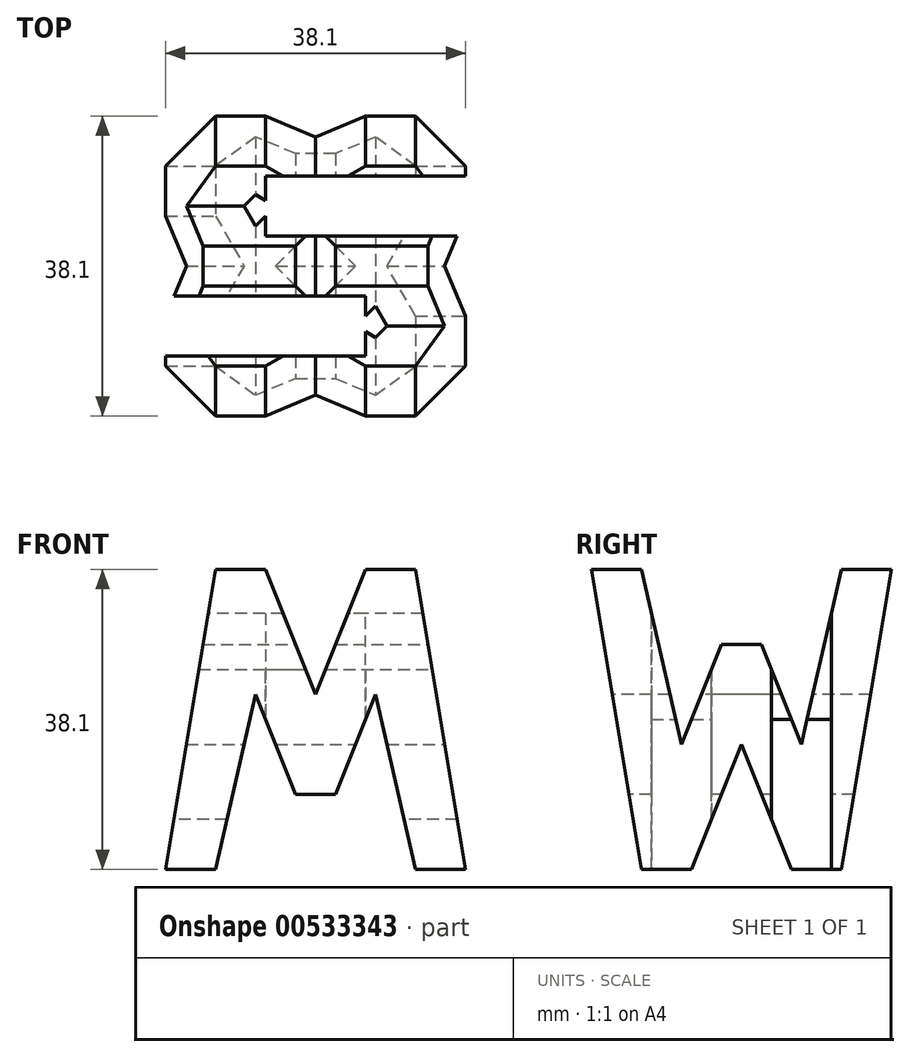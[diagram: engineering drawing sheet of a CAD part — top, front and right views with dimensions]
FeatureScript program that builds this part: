
annotation { "Feature Type Name" : "Feature", "Feature Type Description" : "" }
export const myFeature = defineFeature(function(context is Context, id is Id, definition is map)
    precondition{}
    {
        {
            var Q0;
            Q0=qCreatedBy(makeId("Front.planeOp"),FACE);
            var sketch = newSketch(context, id + "F0", { "sketchPlane" : qUnion([Q0])});
            skLineSegment(sketch, "E0", {"start": v(0, 0) * mm, "end": v(0, 38.1) * mm});
            skLineSegment(sketch, "E1", {"start": v(0, 38.1) * mm, "end": v(38.1, 38.1) * mm});
            skLineSegment(sketch, "E2", {"start": v(38.1, 38.1) * mm, "end": v(38.1, 0) * mm});
            skLineSegment(sketch, "E3", {"start": v(0, 0) * mm, "end": v(38.1, 0) * mm});
            skSolve(sketch);
        }
        {
            var Q0;
            Q0 = qSketchRegion(id + "F0", true);
            extrude(context, id + "F1", {"entities" : qUnion([Q0]), "depth" : 38.1 * mm, "offsetDistance" : 25.4 * mm});
        }
        {
            var Q0;
            Q0=qCreatedBy(makeId("Front.planeOp"),FACE);
            cPlane(context, id + "F2", {"entities" : qUnion([Q0]), "cplaneType" : CPlaneType.OFFSET, "offset" : 38.1 * mm, "width" : 152.4 * mm, "height" : 152.4 * mm});
        }
        {
            var Q0;
            Q0=qCreatedBy(makeId("Right.planeOp"),FACE);
            cPlane(context, id + "F3", {"entities" : qUnion([Q0]), "cplaneType" : CPlaneType.OFFSET, "offset" : 38.1 * mm, "width" : 152.4 * mm, "height" : 152.4 * mm});
        }
        {
            var Q0;
            Q0=qCreatedBy(makeId("Top.planeOp"),FACE);
            cPlane(context, id + "F4", {"entities" : qUnion([Q0]), "cplaneType" : CPlaneType.OFFSET, "offset" : 38.1 * mm, "width" : 152.4 * mm, "height" : 152.4 * mm});
        }
        {
            var Q0;
            Q0=qCreatedBy(id+"F3.planeOp",FACE);
            var sketch = newSketch(context, id + "F5", { "sketchPlane" : qUnion([Q0])});
            skLineSegment(sketch, "E4", {"start": v(-38.1, 38.1) * mm, "end": v(-38.1, 0) * mm});
            skLineSegment(sketch, "E5", {"start": v(-38.1, 0) * mm, "end": v(0, 0) * mm});
            skLineSegment(sketch, "E6", {"start": v(0, 0) * mm, "end": v(0, 38.1) * mm});
            skLineSegment(sketch, "E7", {"start": v(0, 38.1) * mm, "end": v(-38.1, 38.1) * mm});
            skLineSegment(sketch, "E8", {"start": v(-38.1, 38.1) * mm, "end": v(-31.75, 0) * mm});
            skLineSegment(sketch, "E9", {"start": v(-31.75, 0) * mm, "end": v(-25.4, 0) * mm});
            skLineSegment(sketch, "E10", {"start": v(-25.4, 0) * mm, "end": v(-19.05, 15.87) * mm});
            skLineSegment(sketch, "E11", {"start": v(-19.05, 15.87) * mm, "end": v(-12.7, 0) * mm});
            skLineSegment(sketch, "E12", {"start": v(-12.7, 0) * mm, "end": v(-6.35, 0) * mm});
            skLineSegment(sketch, "E13", {"start": v(-6.35, 0) * mm, "end": v(0, 38.1) * mm});
            skLineSegment(sketch, "E14", {"start": v(0, 38.1) * mm, "end": v(-6.35, 38.1) * mm});
            skLineSegment(sketch, "E15", {"start": v(-6.35, 38.1) * mm, "end": v(-11.43, 15.87) * mm});
            skLineSegment(sketch, "E16", {"start": v(-11.43, 15.87) * mm, "end": v(-16.51, 28.57) * mm});
            skLineSegment(sketch, "E17", {"start": v(-16.51, 28.57) * mm, "end": v(-21.6, 28.57) * mm});
            skLineSegment(sketch, "E18", {"start": v(-21.6, 28.57) * mm, "end": v(-26.67, 15.87) * mm});
            skLineSegment(sketch, "E19", {"start": v(-26.67, 15.87) * mm, "end": v(-31.75, 38.1) * mm});
            skSolve(sketch);
        }
        {
            var Q0;
            {var subQ0=sQuery(id+"F5.wireOp",EDGE,"E15");Q0=makeQuery(id+"F5.imprint","IMPRINT",FACE,{"disambiguationData":[TD([[makeQuery(id+"F5.imprint","IMPRINT",EDGE,{"derivedFrom":subQ0}),-1.0]])]});}
            var Q1;
            {var subQ0=sQuery(id+"F5.wireOp",EDGE,"E4");Q1=makeQuery(id+"F5.imprint","IMPRINT",FACE,{"disambiguationData":[TD([[makeQuery(id+"F5.imprint","IMPRINT",EDGE,{"derivedFrom":subQ0}),1.0]])]});}
            var Q2;
            {var subQ0=sQuery(id+"F5.wireOp",EDGE,"E10");Q2=makeQuery(id+"F5.imprint","IMPRINT",FACE,{"disambiguationData":[TD([[makeQuery(id+"F5.imprint","IMPRINT",EDGE,{"derivedFrom":subQ0}),-1.0]])]});}
            var Q3;
            {var subQ0=sQuery(id+"F5.wireOp",EDGE,"E6");Q3=makeQuery(id+"F5.imprint","IMPRINT",FACE,{"disambiguationData":[TD([[makeQuery(id+"F5.imprint","IMPRINT",EDGE,{"derivedFrom":subQ0}),1.0]])]});}
            extrude(context, id + "F6", {"entities" : qUnion([Q0, Q1, Q2, Q3]), "operationType" : NewBodyOperationType.REMOVE, "oppositeDirection" : true, "depth" : 38.1 * mm, "offsetDistance" : 25.4 * mm});
        }
        {
            var Q0;
            Q0=qCreatedBy(id+"F2.planeOp",FACE);
            var sketch = newSketch(context, id + "F7", { "sketchPlane" : qUnion([Q0])});
            skLineSegment(sketch, "E20", {"start": v(38.1, 38.1) * mm, "end": v(38.1, 0) * mm});
            skLineSegment(sketch, "E21", {"start": v(38.1, 0) * mm, "end": v(0, 0) * mm});
            skLineSegment(sketch, "E22", {"start": v(0, 0) * mm, "end": v(0, 38.1) * mm});
            skLineSegment(sketch, "E23", {"start": v(0, 38.1) * mm, "end": v(38.1, 38.1) * mm});
            skLineSegment(sketch, "E24", {"start": v(6.35, 38.1) * mm, "end": v(0, 0) * mm});
            skLineSegment(sketch, "E25", {"start": v(6.35, 0) * mm, "end": v(11.43, 22.22) * mm});
            skLineSegment(sketch, "E26", {"start": v(11.43, 22.22) * mm, "end": v(16.51, 9.52) * mm});
            skLineSegment(sketch, "E27", {"start": v(16.51, 9.52) * mm, "end": v(21.6, 9.52) * mm});
            skLineSegment(sketch, "E28", {"start": v(21.6, 9.52) * mm, "end": v(26.67, 22.23) * mm});
            skLineSegment(sketch, "E29", {"start": v(26.67, 22.23) * mm, "end": v(31.75, 0) * mm});
            skLineSegment(sketch, "E30", {"start": v(38.1, 0) * mm, "end": v(31.75, 38.1) * mm});
            skLineSegment(sketch, "E31", {"start": v(25.4, 38.1) * mm, "end": v(19.05, 22.22) * mm});
            skPoint(sketch, "E31.endSnap0", {"position": v(19.05, 9.52) * mm});
            skLineSegment(sketch, "E32", {"start": v(19.05, 22.22) * mm, "end": v(12.7, 38.1) * mm});
            skSolve(sketch);
        }
        {
            var Q0;
            {var subQ0=sQuery(id+"F7.wireOp",EDGE,"E22");Q0=makeQuery(id+"F7.imprint","IMPRINT",FACE,{"disambiguationData":[TD([[makeQuery(id+"F7.imprint","IMPRINT",EDGE,{"derivedFrom":subQ0}),-1.0]])]});}
            var Q1;
            {var subQ0=sQuery(id+"F7.wireOp",EDGE,"E31");Q1=makeQuery(id+"F7.imprint","IMPRINT",FACE,{"disambiguationData":[TD([[makeQuery(id+"F7.imprint","IMPRINT",EDGE,{"derivedFrom":subQ0}),-1.0]])]});}
            var Q2;
            {var subQ0=sQuery(id+"F7.wireOp",EDGE,"E20");Q2=makeQuery(id+"F7.imprint","IMPRINT",FACE,{"disambiguationData":[TD([[makeQuery(id+"F7.imprint","IMPRINT",EDGE,{"derivedFrom":subQ0}),-1.0]])]});}
            var Q3;
            {var subQ0=sQuery(id+"F7.wireOp",EDGE,"E25");Q3=makeQuery(id+"F7.imprint","IMPRINT",FACE,{"disambiguationData":[TD([[makeQuery(id+"F7.imprint","IMPRINT",EDGE,{"derivedFrom":subQ0}),-1.0]])]});}
            extrude(context, id + "F8", {"entities" : qUnion([Q0, Q1, Q2, Q3]), "operationType" : NewBodyOperationType.REMOVE, "oppositeDirection" : true, "depth" : 38.1 * mm, "offsetDistance" : 25.4 * mm});
        }
        {
            var Q0;
            Q0=qCreatedBy(id+"F4.planeOp",FACE);
            var sketch = newSketch(context, id + "F9", { "sketchPlane" : qUnion([Q0])});
            skLineSegment(sketch, "E33", {"start": v(38.1, 0) * mm, "end": v(38.1, -38.1) * mm});
            skLineSegment(sketch, "E34", {"start": v(38.1, -38.1) * mm, "end": v(0, -38.1) * mm});
            skLineSegment(sketch, "E35", {"start": v(0, -38.1) * mm, "end": v(0, 0) * mm});
            skLineSegment(sketch, "E36", {"start": v(0, 0) * mm, "end": v(38.1, 0) * mm});
            skLineSegment(sketch, "E37", {"start": v(38.1, -7.62) * mm, "end": v(12.7, -7.62) * mm});
            skLineSegment(sketch, "E38", {"start": v(0, -22.86) * mm, "end": v(25.4, -22.86) * mm});
            skLineSegment(sketch, "E39", {"start": v(25.4, -22.86) * mm, "end": v(25.4, -30.48) * mm});
            skLineSegment(sketch, "E40", {"start": v(25.4, -30.48) * mm, "end": v(0, -30.48) * mm});
            skLineSegment(sketch, "E41", {"start": v(12.7, -7.62) * mm, "end": v(12.7, -15.24) * mm});
            skLineSegment(sketch, "E42", {"start": v(12.7, -15.24) * mm, "end": v(38.1, -15.24) * mm});
            skSolve(sketch);
        }
        {
            var Q0;
            {var subQ0=sQuery(id+"F9.wireOp",EDGE,"E37");Q0=makeQuery(id+"F9.imprint","IMPRINT",FACE,{"disambiguationData":[TD([[makeQuery(id+"F9.imprint","IMPRINT",EDGE,{"derivedFrom":subQ0}),1.0]])]});}
            var Q1;
            {var subQ0=sQuery(id+"F9.wireOp",EDGE,"E38");Q1=makeQuery(id+"F9.imprint","IMPRINT",FACE,{"disambiguationData":[TD([[makeQuery(id+"F9.imprint","IMPRINT",EDGE,{"derivedFrom":subQ0}),-1.0]])]});}
            extrude(context, id + "F10", {"entities" : qUnion([Q0, Q1]), "operationType" : NewBodyOperationType.REMOVE, "oppositeDirection" : true, "depth" : 38.1 * mm, "offsetDistance" : 25.4 * mm});
        }
    });
